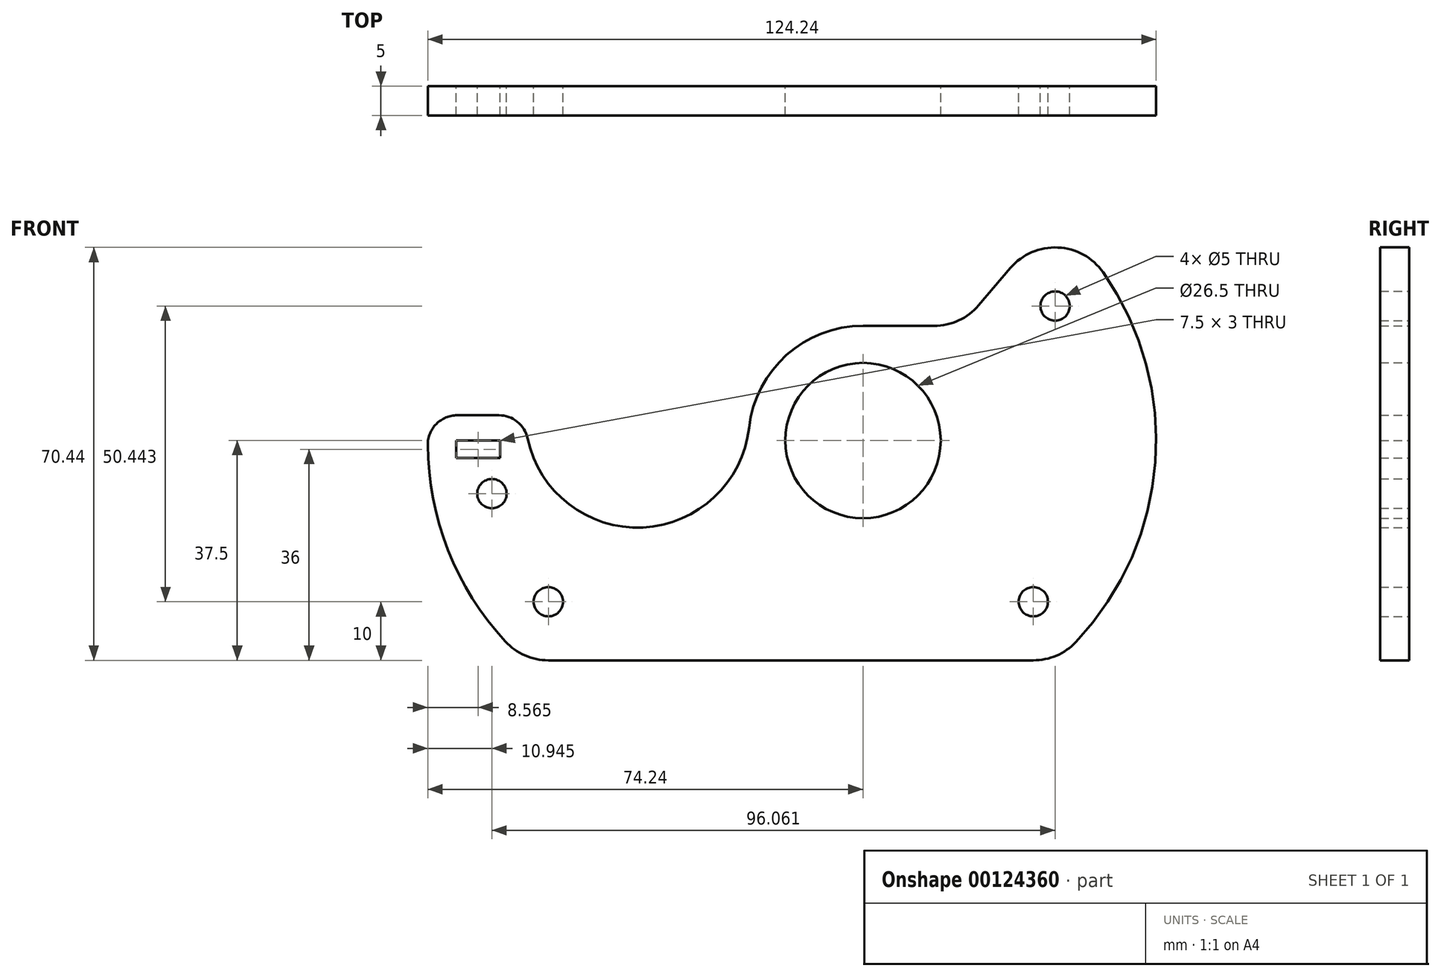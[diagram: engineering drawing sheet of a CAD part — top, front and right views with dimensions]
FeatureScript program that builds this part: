
annotation { "Feature Type Name" : "Feature", "Feature Type Description" : "" }
export const myFeature = defineFeature(function(context is Context, id is Id, definition is map)
    precondition{}
    {
        {
            var Q0;
            Q0=qCreatedBy(makeId("Front.planeOp"),FACE);
            var sketch = newSketch(context, id + "F0", { "sketchPlane" : qUnion([Q0])});
            skCircle(sketch, "E0", {"center": v(0, 0) * mm, "radius": 12.5 * mm, "construction": true});
            skCircle(sketch, "E1", {"center": v(0, 0) * mm, "radius": 30 * mm, "construction": true});
            skCircle(sketch, "E2", {"center": v(0, 0) * mm, "radius": 13.25 * mm});
            skLineSegment(sketch, "E3.bottom", {"start": v(29.05, -37.5) * mm, "end": v(-53.67, -37.5) * mm});
            skPoint(sketch, "E4.orphan", {"position": v(50, 37.5) * mm});
            skPoint(sketch, "E5.orphan", {"position": v(50, -37.5) * mm});
            skArc(sketch, "E6.trimOffspring", {"start": v(36.3, -34.37) * mm, "mid": v(49.86, -3.68) * mm, "end": v(40.96, 28.68) * mm});
            skArc(sketch, "E7", {"start": v(-74.24, -0.72) * mm, "mid": v(-70.76, -18.73) * mm, "end": v(-61.03, -34.27) * mm});
            skLineSegment(sketch, "E8", {"start": v(-69.24, 4.3) * mm, "end": v(-62.1, 4.3) * mm});
            skPoint(sketch, "E9.orphan", {"position": v(-50, 37.5) * mm});
            skPoint(sketch, "E10.orphan", {"position": v(-50, -37.5) * mm});
            skPoint(sketch, "E11.orphan", {"position": v(-60, 34.54) * mm});
            skLineSegment(sketch, "E12", {"start": v(0, 0) * mm, "end": v(32.77, 22.94) * mm, "construction": true});
            skLineSegment(sketch, "E13", {"start": v(0, 0) * mm, "end": v(32.77, -22.94) * mm, "construction": true});
            skLineSegment(sketch, "E14", {"start": v(0, 0) * mm, "end": v(-36.96, -15.3) * mm, "construction": true});
            skLineSegment(sketch, "E15", {"start": v(0, 0) * mm, "end": v(-27.02, -29.5) * mm, "construction": true});
            skLineSegment(sketch, "E16", {"start": v(0, 0) * mm, "end": v(8.07, 10.51) * mm});
            skPoint(sketch, "E17.visualSharp", {"position": v(-34.89, 19.57) * mm});
            skPoint(sketch, "E18.visualSharp", {"position": v(15.02, 19.57) * mm});
            skPoint(sketch, "E19.visualSharp", {"position": v(33.07, -37.5) * mm});
            skArc(sketch, "E19.filletArc", {"start": v(29.05, -37.5) * mm, "mid": v(33, -36.69) * mm, "end": v(36.3, -34.37) * mm});
            skArc(sketch, "E20.filletArc", {"start": v(-61.03, -34.27) * mm, "mid": v(-57.69, -36.66) * mm, "end": v(-53.67, -37.5) * mm});
            skArc(sketch, "E21", {"start": v(40.96, 28.68) * mm, "mid": v(33.25, 32.93) * mm, "end": v(25.16, 29.44) * mm});
            skLineSegment(sketch, "E22", {"start": v(0, 0) * mm, "end": v(8.6, 10.07) * mm});
            skLineSegment(sketch, "E23.trimOffspring", {"start": v(19.72, 23.07) * mm, "end": v(25.16, 29.44) * mm});
            skPoint(sketch, "E24.visualSharp", {"position": v(16.73, 19.57) * mm});
            skArc(sketch, "E24.filletArc", {"start": v(12.12, 19.57) * mm, "mid": v(16.3, 20.49) * mm, "end": v(19.72, 23.07) * mm});
            skPoint(sketch, "E25.visualSharp", {"position": v(-58.48, 4.3) * mm});
            skCircle(sketch, "E26", {"center": v(32.77, 22.94) * mm, "radius": 2.5 * mm});
            skCircle(sketch, "E27", {"center": v(29.05, -27.5) * mm, "radius": 2.5 * mm});
            skCircle(sketch, "E28", {"center": v(-53.67, -27.5) * mm, "radius": 2.5 * mm});
            skCircle(sketch, "E29", {"center": v(-24.24, -0.4) * mm, "radius": 40 * mm, "construction": true});
            skCircle(sketch, "E30", {"center": v(-63.3, -9.06) * mm, "radius": 2.5 * mm});
            skPoint(sketch, "E31.visualSharp", {"position": v(-74.02, 4.3) * mm});
            skArc(sketch, "E31.filletArc", {"start": v(-69.24, 4.3) * mm, "mid": v(-72.79, 2.83) * mm, "end": v(-74.24, -0.72) * mm});
            skArc(sketch, "E32", {"start": v(0, 19.57) * mm, "mid": v(-13.04, 14.59) * mm, "end": v(-19.45, 2.18) * mm});
            skLineSegment(sketch, "E33.trimOffspring", {"start": v(0, 19.57) * mm, "end": v(12.12, 19.57) * mm});
            skPoint(sketch, "E34.visualSharp", {"position": v(-19.09, 4.3) * mm});
            skPoint(sketch, "E35.visualSharp", {"position": v(-18.48, 4.3) * mm});
            skLineSegment(sketch, "E36", {"start": v(-24.24, -0.4) * mm, "end": v(-53.67, -27.5) * mm, "construction": true});
            skLineSegment(sketch, "E37", {"start": v(-24.24, -0.4) * mm, "end": v(-63.3, -9.06) * mm, "construction": true});
            skArc(sketch, "E38", {"start": v(-57.22, 0.34) * mm, "mid": v(-37.55, -14.82) * mm, "end": v(-19.45, 2.18) * mm});
            skPoint(sketch, "E39.orphan", {"position": v(-62.97, 4.3) * mm});
            skPoint(sketch, "E40.visualSharp", {"position": v(-57.63, 4.3) * mm});
            skArc(sketch, "E40.filletArc", {"start": v(-57.22, 0.34) * mm, "mid": v(-58.96, 3.2) * mm, "end": v(-62.1, 4.3) * mm});
            skLineSegment(sketch, "E41", {"start": v(-65.67, 4.3) * mm, "end": v(-65.67, -5.15) * mm, "construction": true});
            skLineSegment(sketch, "E42.bottom", {"start": v(-61.92, -3) * mm, "end": v(-69.42, -3) * mm});
            skLineSegment(sketch, "E42.top", {"start": v(-61.92, 0) * mm, "end": v(-69.42, 0) * mm});
            skLineSegment(sketch, "E42.left", {"start": v(-61.92, -3) * mm, "end": v(-61.92, 0) * mm});
            skLineSegment(sketch, "E42.right", {"start": v(-69.42, -3) * mm, "end": v(-69.42, 0) * mm});
            skPoint(sketch, "E42.middle", {"position": v(-65.67, -1.5) * mm});
            skSolve(sketch);
        }
        {
            var Q0;
            Q0=makeQuery(id+"F0.imprint","IMPRINT",FACE,{"disambiguationData":[TD([[makeQuery(id+"F0.imprint","IMPRINT",EDGE,{"derivedFrom":sQuery(id+"F0.wireOp",EDGE,"E3.bottom")}),-1.0]])]});
            extrude(context, id + "F1", {"entities" : qUnion([Q0]), "depth" : 5 * mm});
        }
    });
